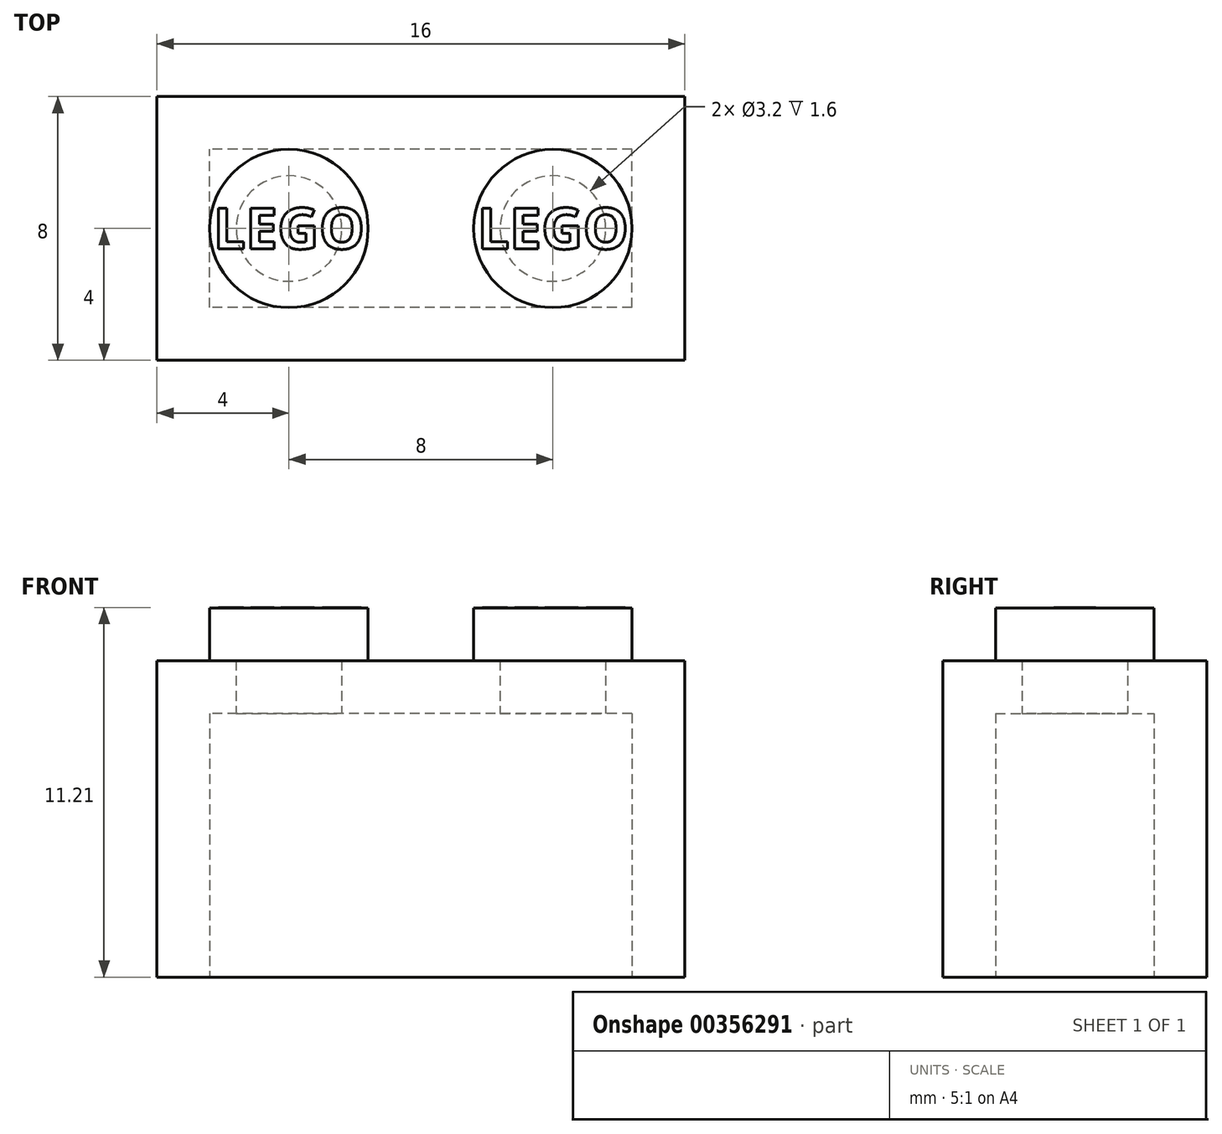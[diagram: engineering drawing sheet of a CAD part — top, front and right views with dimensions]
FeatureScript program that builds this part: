
annotation { "Feature Type Name" : "Feature", "Feature Type Description" : "" }
export const myFeature = defineFeature(function(context is Context, id is Id, definition is map)
    precondition{}
    {
        {
            var Q0;
            Q0=qCreatedBy(makeId("Top.planeOp"),FACE);
            var sketch = newSketch(context, id + "F0", { "sketchPlane" : qUnion([Q0])});
            skLineSegment(sketch, "E0.bottom", {"start": v(-8, 4) * mm, "end": v(8, 4) * mm});
            skLineSegment(sketch, "E0.top", {"start": v(-8, -4) * mm, "end": v(8, -4) * mm});
            skLineSegment(sketch, "E0.left", {"start": v(-8, 4) * mm, "end": v(-8, -4) * mm});
            skLineSegment(sketch, "E0.right", {"start": v(8, 4) * mm, "end": v(8, -4) * mm});
            skPoint(sketch, "E0.middle", {"position": v(0, 0) * mm});
            skSolve(sketch);
        }
        {
            var Q0;
            Q0=makeQuery(id+"F0.imprint","IMPRINT",FACE,{"disambiguationData":[TD([[makeQuery(id+"F0.imprint","IMPRINT",EDGE,{"derivedFrom":sQuery(id+"F0.wireOp",EDGE,"E0.bottom")}),-1.0]])]});
            extrude(context, id + "F1", {"entities" : qUnion([Q0]), "depth" : 9.6 * mm});
        }
        {
            var Q0;
            Q0=makeQuery(id+"F1.opExtrude","CAP_FACE",FACE,{"disambiguationData":[OSD([sQuery(id+"F0.wireOp",EDGE,"E0.bottom"),sQuery(id+"F0.wireOp",EDGE,"E0.top"),sQuery(id+"F0.wireOp",EDGE,"E0.left"),sQuery(id+"F0.wireOp",EDGE,"E0.right")])],"isStart":true});
            var sketch = newSketch(context, id + "F2", { "sketchPlane" : qUnion([Q0])});
            skLineSegment(sketch, "E1.bottom", {"start": v(6.4, 2.4) * mm, "end": v(-6.4, 2.4) * mm});
            skLineSegment(sketch, "E1.top", {"start": v(6.4, -2.4) * mm, "end": v(-6.4, -2.4) * mm});
            skLineSegment(sketch, "E1.left", {"start": v(6.4, 2.4) * mm, "end": v(6.4, -2.4) * mm});
            skLineSegment(sketch, "E1.right", {"start": v(-6.4, 2.4) * mm, "end": v(-6.4, -2.4) * mm});
            skPoint(sketch, "E1.middle", {"position": v(0, 0) * mm});
            skSolve(sketch);
        }
        {
            var Q0;
            Q0=makeQuery(id+"F2.imprint","IMPRINT",FACE,{"disambiguationData":[TD([[makeQuery(id+"F2.imprint","IMPRINT",EDGE,{"derivedFrom":sQuery(id+"F2.wireOp",EDGE,"E1.bottom")}),1.0]])]});
            extrude(context, id + "F3", {"entities" : qUnion([Q0]), "operationType" : NewBodyOperationType.REMOVE, "oppositeDirection" : true, "depth" : 8 * mm});
        }
        {
            var Q0;
            Q0=makeQuery(id+"F3.boolean.opBoolean","COPY",FACE,{"derivedFrom":makeQuery(id+"F3.opExtrude","CAP_FACE",FACE,{"disambiguationData":[OSD([sQuery(id+"F2.wireOp",EDGE,"E1.bottom"),sQuery(id+"F2.wireOp",EDGE,"E1.top"),sQuery(id+"F2.wireOp",EDGE,"E1.left"),sQuery(id+"F2.wireOp",EDGE,"E1.right")])],"isStart":false})});
            var sketch = newSketch(context, id + "F4", { "sketchPlane" : qUnion([Q0])});
            skCircle(sketch, "E2", {"center": v(-4, 0) * mm, "radius": 1.6 * mm});
            skCircle(sketch, "E3", {"center": v(4, 0) * mm, "radius": 1.6 * mm});
            skSolve(sketch);
        }
        {
            var Q0;
            Q0=makeQuery(id+"F4.imprint","IMPRINT",FACE,{"disambiguationData":[TD([[makeQuery(id+"F4.imprint","IMPRINT",EDGE,{"derivedFrom":sQuery(id+"F4.wireOp",EDGE,"E2")}),1.0]])]});
            var Q1;
            Q1=makeQuery(id+"F4.imprint","IMPRINT",FACE,{"disambiguationData":[TD([[makeQuery(id+"F4.imprint","IMPRINT",EDGE,{"derivedFrom":sQuery(id+"F4.wireOp",EDGE,"E3")}),1.0]])]});
            extrude(context, id + "F5", {"entities" : qUnion([Q0, Q1]), "operationType" : NewBodyOperationType.REMOVE, "oppositeDirection" : true, "depth" : 1.6 * mm});
        }
        {
            var Q0;
            Q0=makeQuery(id+"F1.opExtrude","CAP_FACE",FACE,{"disambiguationData":[OSD([sQuery(id+"F0.wireOp",EDGE,"E0.bottom"),sQuery(id+"F0.wireOp",EDGE,"E0.top"),sQuery(id+"F0.wireOp",EDGE,"E0.left"),sQuery(id+"F0.wireOp",EDGE,"E0.right")])],"isStart":false});
            var sketch = newSketch(context, id + "F6", { "sketchPlane" : qUnion([Q0])});
            skCircle(sketch, "E4", {"center": v(-4, 0) * mm, "radius": 2.4 * mm});
            skCircle(sketch, "E5", {"center": v(4, 0) * mm, "radius": 2.4 * mm});
            skSolve(sketch);
        }
        {
            var Q0;
            Q0 = qSketchRegion(id + "F6", true);
            extrude(context, id + "F7", {"entities" : qUnion([Q0]), "operationType" : NewBodyOperationType.ADD, "depth" : 1.6 * mm});
        }
        {
            var Q0;
            Q0=makeQuery(id+"F7.opExtrude","CAP_FACE",FACE,{"disambiguationData":[OSD([sQuery(id+"F6.wireOp",EDGE,"E4")])],"isStart":false});
            var sketch = newSketch(context, id + "F8", { "sketchPlane" : qUnion([Q0])});
            skText(sketch, "E6", { "text": "LEGO\n", "fontName": "OpenSans-Bold.ttf"});
            skText(sketch, "E7", { "text": "LEGO", "fontName": "OpenSans-Bold.ttf"});
            const initialGuessF8  = {"E6": [-0.0063, -0.00062, 1, 0, 0.00125], "E7": [0.0017, -0.00062, 1, 0, 0.00125]};
            skSetInitialGuess(sketch, initialGuessF8);
            skSolve(sketch);
        }
        {
            var Q0;
            Q0 = qSketchRegion(id + "F8", true);
            extrude(context, id + "F9", {"entities" : qUnion([Q0]), "operationType" : NewBodyOperationType.ADD, "depth" : 0.01 * mm});
        }
    });
